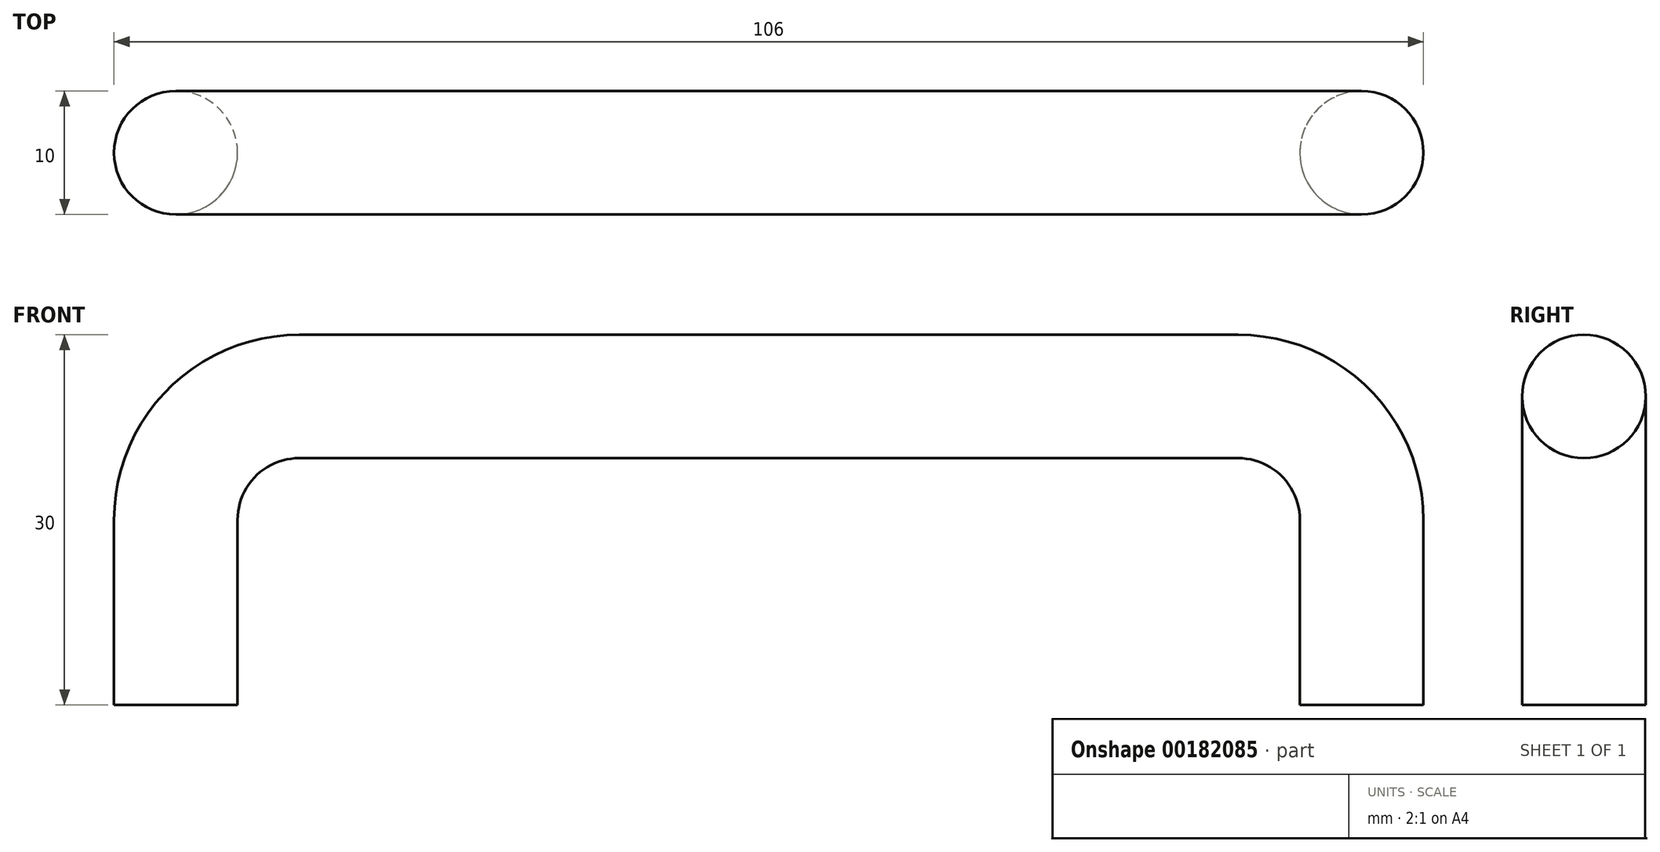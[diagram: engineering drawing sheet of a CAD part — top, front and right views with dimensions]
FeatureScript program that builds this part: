
annotation { "Feature Type Name" : "Feature", "Feature Type Description" : "" }
export const myFeature = defineFeature(function(context is Context, id is Id, definition is map)
    precondition{}
    {
        {
            var Q0;
            Q0=qCreatedBy(makeId("Front.planeOp"),FACE);
            var sketch = newSketch(context, id + "F0", { "sketchPlane" : qUnion([Q0])});
            skLineSegment(sketch, "E0", {"start": v(0, 0) * mm, "end": v(0, 15) * mm});
            skLineSegment(sketch, "E1", {"start": v(10, 25) * mm, "end": v(86, 25) * mm});
            skLineSegment(sketch, "E2", {"start": v(96, 15) * mm, "end": v(96, 0) * mm});
            skPoint(sketch, "E3.visualSharp", {"position": v(0, 25) * mm});
            skArc(sketch, "E3.filletArc", {"start": v(10, 25) * mm, "mid": v(2.93, 22.07) * mm, "end": v(0, 15) * mm});
            skPoint(sketch, "E4.visualSharp", {"position": v(96, 25) * mm});
            skArc(sketch, "E4.filletArc", {"start": v(96, 15) * mm, "mid": v(93.07, 22.07) * mm, "end": v(86, 25) * mm});
            skSolve(sketch);
        }
        {
            var Q0;
            Q0=qCreatedBy(makeId("Top.planeOp"),FACE);
            var sketch = newSketch(context, id + "F1", { "sketchPlane" : qUnion([Q0])});
            skCircle(sketch, "E5", {"center": v(0, 0) * mm, "radius": 5 * mm});
            skSolve(sketch);
        }
        {
            var Q0;
            Q0=makeQuery(id+"F1.imprint","IMPRINT",FACE,{"disambiguationData":[TD([[makeQuery(id+"F1.imprint","IMPRINT",EDGE,{"derivedFrom":sQuery(id+"F1.wireOp",EDGE,"E5")}),1.0]])]});
            var Q1;
            Q1 = qConstructionFilter(qBodyType(qCreatedBy(id + "F0" ,EDGE), BodyType.WIRE), ConstructionObject.NO);
            sweep(context, id + "F2", {"profiles" : qUnion([Q0]), "path" : qUnion([Q1])});
        }
    });
